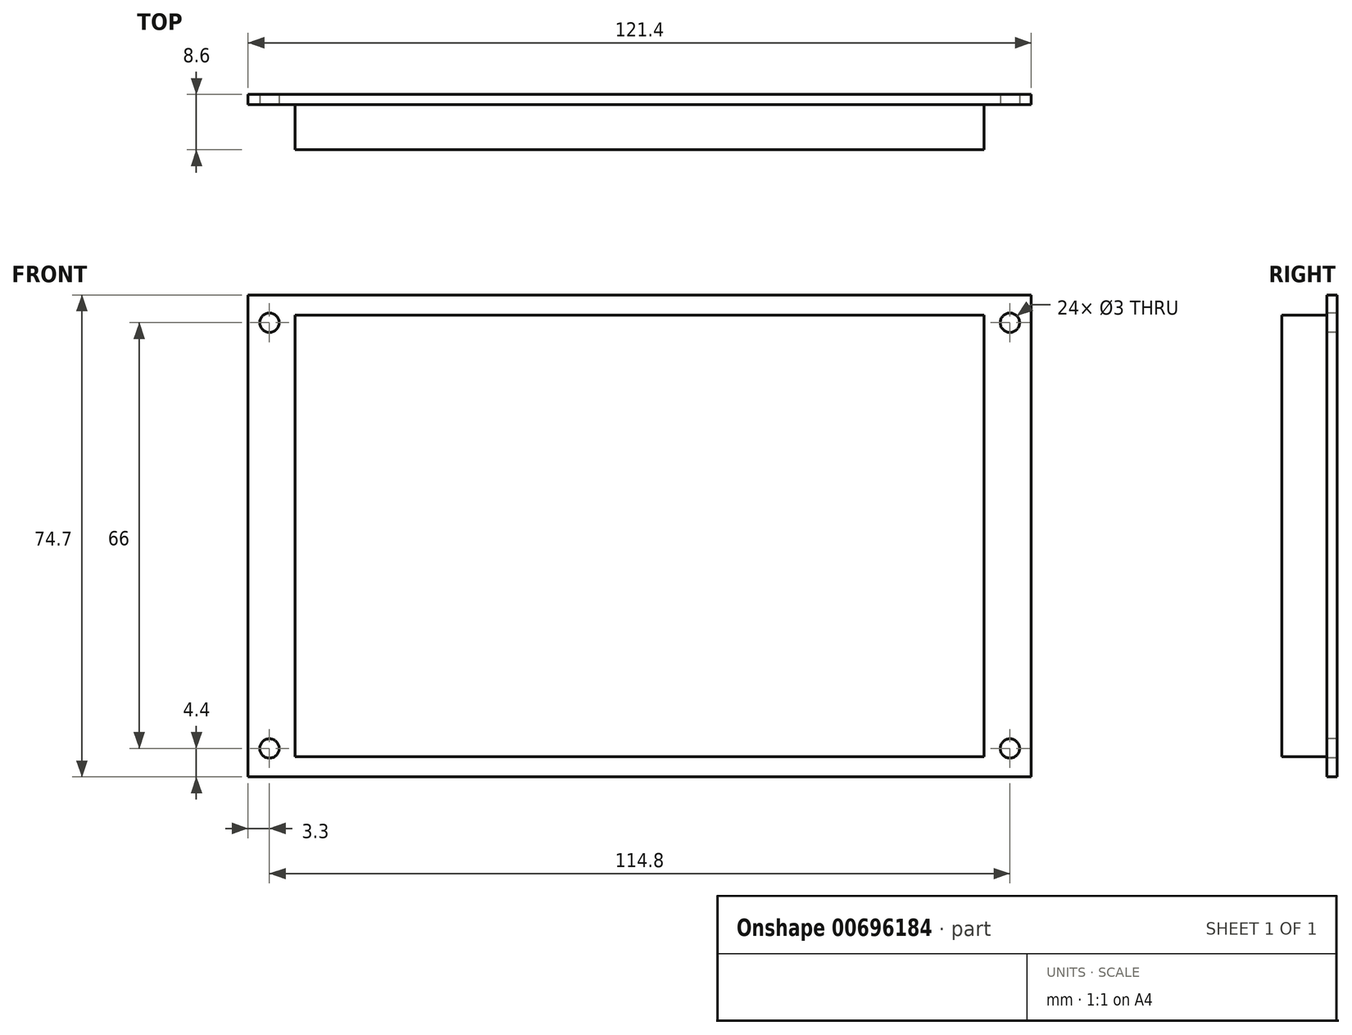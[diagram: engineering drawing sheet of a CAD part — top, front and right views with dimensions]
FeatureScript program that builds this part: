
annotation { "Feature Type Name" : "Feature", "Feature Type Description" : "" }
export const myFeature = defineFeature(function(context is Context, id is Id, definition is map)
    precondition{}
    {
        {
            var Q0;
            Q0=qCreatedBy(makeId("Front.planeOp"),FACE);
            var sketch = newSketch(context, id + "F0", { "sketchPlane" : qUnion([Q0])});
            skLineSegment(sketch, "E0.bottom", {"start": v(60.7, -37.35) * mm, "end": v(-60.7, -37.35) * mm});
            skLineSegment(sketch, "E0.top", {"start": v(60.7, 37.35) * mm, "end": v(-60.7, 37.35) * mm});
            skLineSegment(sketch, "E0.left", {"start": v(60.7, -37.35) * mm, "end": v(60.7, 37.35) * mm});
            skLineSegment(sketch, "E0.right", {"start": v(-60.7, -37.35) * mm, "end": v(-60.7, 37.35) * mm});
            skPoint(sketch, "E0.middle", {"position": v(0, 0) * mm});
            skCircle(sketch, "E1", {"center": v(-57.4, 33.05) * mm, "radius": 1.5 * mm});
            skCircle(sketch, "E2", {"center": v(57.4, 33.05) * mm, "radius": 1.5 * mm});
            skCircle(sketch, "E3", {"center": v(-57.4, -32.95) * mm, "radius": 1.5 * mm});
            skCircle(sketch, "E4", {"center": v(57.4, -32.95) * mm, "radius": 1.5 * mm});
            skSolve(sketch);
        }
        {
            var Q0;
            Q0=makeQuery(id+"F0.imprint","IMPRINT",FACE,{"disambiguationData":[TD([[makeQuery(id+"F0.imprint","IMPRINT",EDGE,{"derivedFrom":sQuery(id+"F0.wireOp",EDGE,"E0.bottom")}),-1.0]])]});
            extrude(context, id + "F1", {"entities" : qUnion([Q0]), "oppositeDirection" : true, "depth" : 1.6 * mm, "offsetDistance" : 25 * mm});
        }
        {
            var Q0;
            Q0=makeQuery(id+"F1.opExtrude","CAP_FACE",FACE,{"disambiguationData":[OSD([sQuery(id+"F0.wireOp",EDGE,"E0.bottom"),sQuery(id+"F0.wireOp",EDGE,"E0.top"),sQuery(id+"F0.wireOp",EDGE,"E0.left"),sQuery(id+"F0.wireOp",EDGE,"E0.right"),sQuery(id+"F0.wireOp",EDGE,"E1"),sQuery(id+"F0.wireOp",EDGE,"E2"),sQuery(id+"F0.wireOp",EDGE,"E3"),sQuery(id+"F0.wireOp",EDGE,"E4")])],"isStart":true});
            var sketch = newSketch(context, id + "F2", { "sketchPlane" : qUnion([Q0])});
            skLineSegment(sketch, "E5.bottom", {"start": v(53.4, -34.2) * mm, "end": v(-53.4, -34.2) * mm});
            skLineSegment(sketch, "E5.top", {"start": v(53.4, 34.2) * mm, "end": v(-53.4, 34.2) * mm});
            skLineSegment(sketch, "E5.left", {"start": v(53.4, -34.2) * mm, "end": v(53.4, 34.2) * mm});
            skLineSegment(sketch, "E5.right", {"start": v(-53.4, -34.2) * mm, "end": v(-53.4, 34.2) * mm});
            skPoint(sketch, "E5.middle", {"position": v(0, 0) * mm});
            skSolve(sketch);
        }
        {
            var Q0;
            Q0=makeQuery(id+"F2.imprint","IMPRINT",FACE,{"disambiguationData":[TD([[makeQuery(id+"F2.imprint","IMPRINT",EDGE,{"derivedFrom":sQuery(id+"F2.wireOp",EDGE,"E5.bottom")}),-1.0]])]});
            extrude(context, id + "F3", {"entities" : qUnion([Q0]), "depth" : 7 * mm, "offsetDistance" : 25 * mm});
        }
    });
